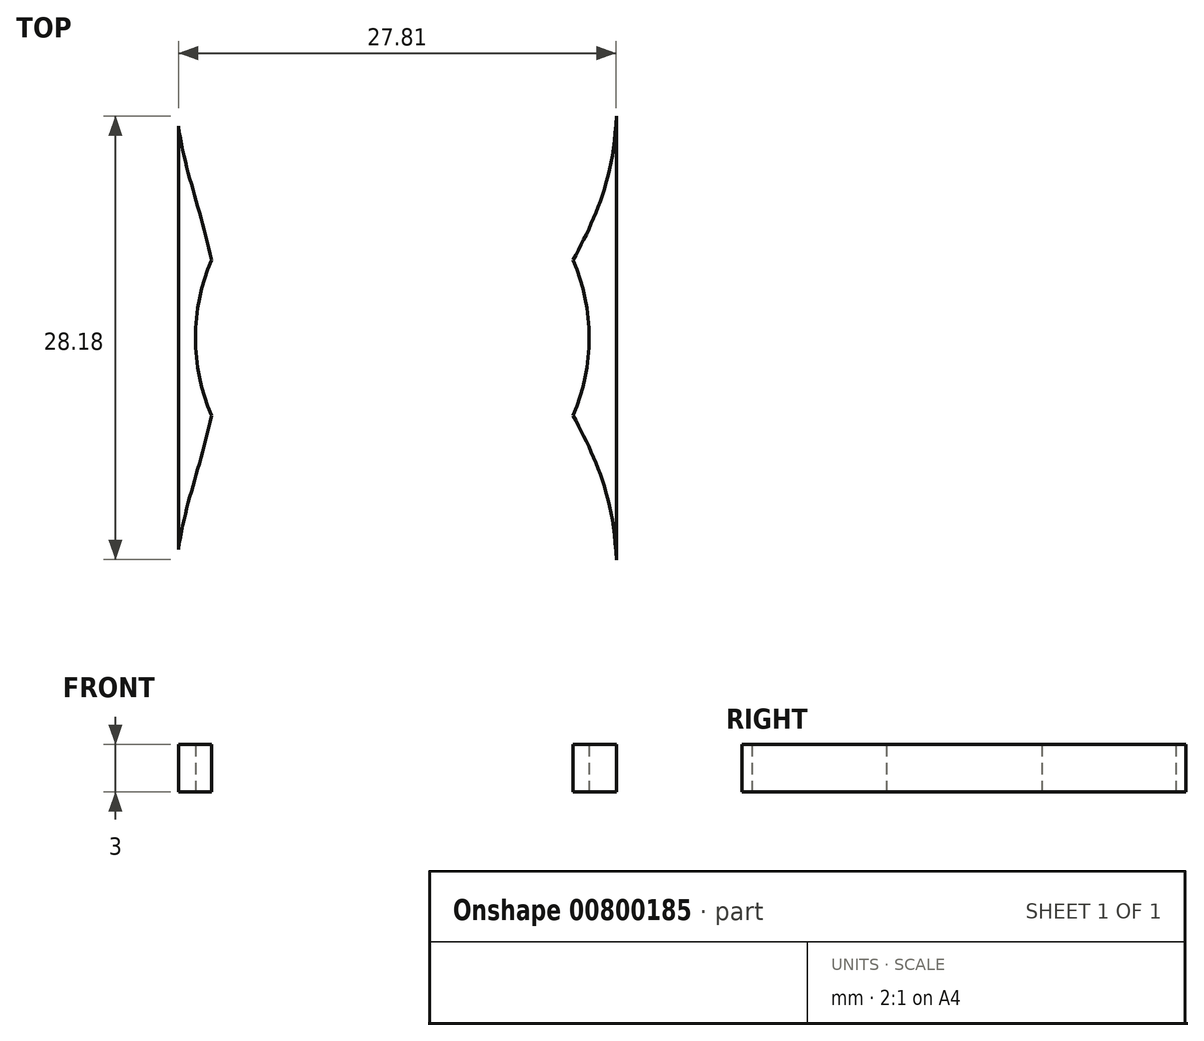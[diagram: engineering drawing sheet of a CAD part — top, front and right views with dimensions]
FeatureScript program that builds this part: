
annotation { "Feature Type Name" : "Feature", "Feature Type Description" : "" }
export const myFeature = defineFeature(function(context is Context, id is Id, definition is map)
    precondition{}
    {
        {
            var Q0;
            Q0=qCreatedBy(makeId("Top.planeOp"),FACE);
            var sketch = newSketch(context, id + "F0", { "sketchPlane" : qUnion([Q0])});
            skArc(sketch, "E0", {"start": v(11, 0) * mm, "mid": v(0, 11) * mm, "end": v(-11, 0) * mm});
            skArc(sketch, "E1", {"start": v(12.5, 0) * mm, "mid": v(0, 12.5) * mm, "end": v(-12.5, 0) * mm});
            skCircle(sketch, "E2", {"center": v(0, 35) * mm, "radius": 9.95 * mm});
            skFitSpline(sketch, "E3", {"points": [v(-6.79, 58.74) * mm, v(-11.6, 70.67) * mm, v(-10.4, 72.78) * mm, v(-3.48, 59.94) * mm, v(-6.79, 58.74) * mm]});
            skFitSpline(sketch, "E4.MirrorC", {"points": [v(6.79, 58.74) * mm, v(11.6, 70.67) * mm, v(10.4, 72.78) * mm, v(3.48, 59.94) * mm, v(6.79, 58.74) * mm]});
            skFitSpline(sketch, "E5", {"points": [v(-3.48, 59.94) * mm, v(3.48, 59.94) * mm, v(6.79, 58.74) * mm, v(13.6, 45.57) * mm, v(14.22, 33.4) * mm, v(14.67, 34.12) * mm], "startDerivative": vector(37.24, 0.89) * mm, "endDerivative": vector(-5.73, 16.07) * mm});
            skFitSpline(sketch, "E6", {"points": [v(-6.79, 58.74) * mm, v(-11.44, 47.8) * mm, v(-13.59, 35) * mm], "startDerivative": vector(-11.06, -19.84) * mm, "endDerivative": vector(-2.66, -25.56) * mm});
            skFitSpline(sketch, "E7", {"points": [v(14.22, 33.4) * mm, v(23.97, 25.62) * mm, v(28.62, 20.6) * mm, v(21.1, 19.9) * mm, v(14.22, 25.97) * mm, v(14.22, 14.1) * mm, v(11.48, 4.94) * mm], "startDerivative": vector(47.45, -36.92) * mm, "endDerivative": vector(-23.33, -44.45) * mm});
            skFitSpline(sketch, "E8", {"points": [v(-13.59, 35) * mm, v(-23.25, 28.84) * mm, v(-26.82, 25.97) * mm, v(-22.53, 21.68) * mm, v(-13.59, 25.97) * mm], "startDerivative": vector(-33.2, -22.98) * mm, "endDerivative": vector(32.3, 25.98) * mm});
            skFitSpline(sketch, "E9", {"points": [v(-13.59, 25.97) * mm, v(-13.59, 13.45) * mm, v(-11.48, 4.94) * mm], "startDerivative": vector(-0.89, -24.46) * mm, "endDerivative": vector(4.16, -20.38) * mm});
            skFitSpline(sketch, "E10.trimOffspring", {"points": [v(-3.48, 59.94) * mm, v(3.48, 59.94) * mm, v(6.79, 58.74) * mm, v(13.6, 45.57) * mm, v(14.22, 33.4) * mm, v(14.67, 34.12) * mm], "startDerivative": vector(37.24, 0.89) * mm, "endDerivative": vector(-5.73, 16.07) * mm});
            skPoint(sketch, "E11", {"position": v(-12.5, 0) * mm});
            skPoint(sketch, "E12", {"position": v(-11, 0) * mm});
            skPoint(sketch, "E13", {"position": v(11, 0) * mm});
            skPoint(sketch, "E14", {"position": v(12.5, 0) * mm});
            skCircle(sketch, "E15.MirrorC", {"center": v(0, -35) * mm, "radius": 9.95 * mm});
            skFitSpline(sketch, "E16.MirrorCS", {"points": [v(-3.48, -59.94) * mm, v(3.48, -59.94) * mm, v(6.79, -58.74) * mm, v(13.6, -45.57) * mm, v(14.22, -33.4) * mm, v(14.67, -34.12) * mm], "startDerivative": vector(37.24, -0.89) * mm, "endDerivative": vector(-5.73, -16.07) * mm});
            skFitSpline(sketch, "E17.MirrorCS", {"points": [v(14.22, -33.4) * mm, v(23.97, -25.62) * mm, v(28.62, -20.6) * mm, v(21.1, -19.9) * mm, v(14.22, -25.97) * mm, v(14.22, -14.1) * mm, v(11.48, -4.94) * mm], "startDerivative": vector(47.45, 36.92) * mm, "endDerivative": vector(-23.33, 44.45) * mm});
            skFitSpline(sketch, "E18.MirrorCS", {"points": [v(6.79, -58.74) * mm, v(11.6, -70.67) * mm, v(10.4, -72.78) * mm, v(3.48, -59.94) * mm, v(6.79, -58.74) * mm]});
            skFitSpline(sketch, "E19.MirrorCS", {"points": [v(-6.79, -58.74) * mm, v(-11.6, -70.67) * mm, v(-10.4, -72.78) * mm, v(-3.48, -59.94) * mm, v(-6.79, -58.74) * mm]});
            skFitSpline(sketch, "E20.MirrorCS", {"points": [v(-6.79, -58.74) * mm, v(-11.44, -47.8) * mm, v(-13.59, -35) * mm], "startDerivative": vector(-11.06, 19.84) * mm, "endDerivative": vector(-2.66, 25.56) * mm});
            skFitSpline(sketch, "E21.MirrorCS", {"points": [v(-13.59, -35) * mm, v(-23.25, -28.84) * mm, v(-26.82, -25.97) * mm, v(-22.53, -21.68) * mm, v(-13.59, -25.97) * mm], "startDerivative": vector(-33.2, 22.98) * mm, "endDerivative": vector(32.3, -25.98) * mm});
            skFitSpline(sketch, "E22.MirrorCS", {"points": [v(-13.59, -25.97) * mm, v(-13.59, -13.45) * mm, v(-11.48, -4.94) * mm], "startDerivative": vector(-0.89, 24.46) * mm, "endDerivative": vector(4.16, 20.38) * mm});
            skArc(sketch, "E23.MirrorCS", {"start": v(12.5, 0) * mm, "mid": v(0, -12.5) * mm, "end": v(-12.5, 0) * mm});
            skArc(sketch, "E24.MirrorCS", {"start": v(11, 0) * mm, "mid": v(0, -11) * mm, "end": v(-11, 0) * mm});
            skFitSpline(sketch, "E25.MirrorCS", {"points": [v(-3.48, -59.94) * mm, v(3.48, -59.94) * mm, v(6.79, -58.74) * mm, v(13.6, -45.57) * mm, v(14.22, -33.4) * mm, v(14.67, -34.12) * mm], "startDerivative": vector(37.24, -0.89) * mm, "endDerivative": vector(-5.73, -16.07) * mm});
            skPoint(sketch, "E26", {"position": v(-12.27, 8.03) * mm});
            skLineSegment(sketch, "E27", {"start": v(-13.59, 13.45) * mm, "end": v(-13.59, -13.45) * mm});
            skLineSegment(sketch, "E28", {"start": v(14.22, 14.1) * mm, "end": v(14.22, -14.1) * mm});
            skPoint(sketch, "E29", {"position": v(14.22, 0) * mm});
            skCircle(sketch, "E30", {"center": v(-4.99, 50.93) * mm, "radius": 2 * mm});
            skCircle(sketch, "E31", {"center": v(4.52, 50.93) * mm, "radius": 2 * mm});
            skCircle(sketch, "E32.MirrorC", {"center": v(4.52, -50.93) * mm, "radius": 2 * mm});
            skCircle(sketch, "E33.MirrorC", {"center": v(-4.99, -50.93) * mm, "radius": 2 * mm});
            skSolve(sketch);
        }
        {
            var Q0;
            Q0=makeQuery(id+"F0.imprint","IMPRINT",FACE,{"disambiguationData":[TD([[makeQuery(id+"F0.imprint","IMPRINT",EDGE,{"derivedFrom":sQuery(id+"F0.wireOp",EDGE,"E1")}),-1.0]])]});
            extrude(context, id + "F1", {"entities" : qUnion([Q0]), "depth" : 3 * mm, "offsetDistance" : 25 * mm});
        }
    });
